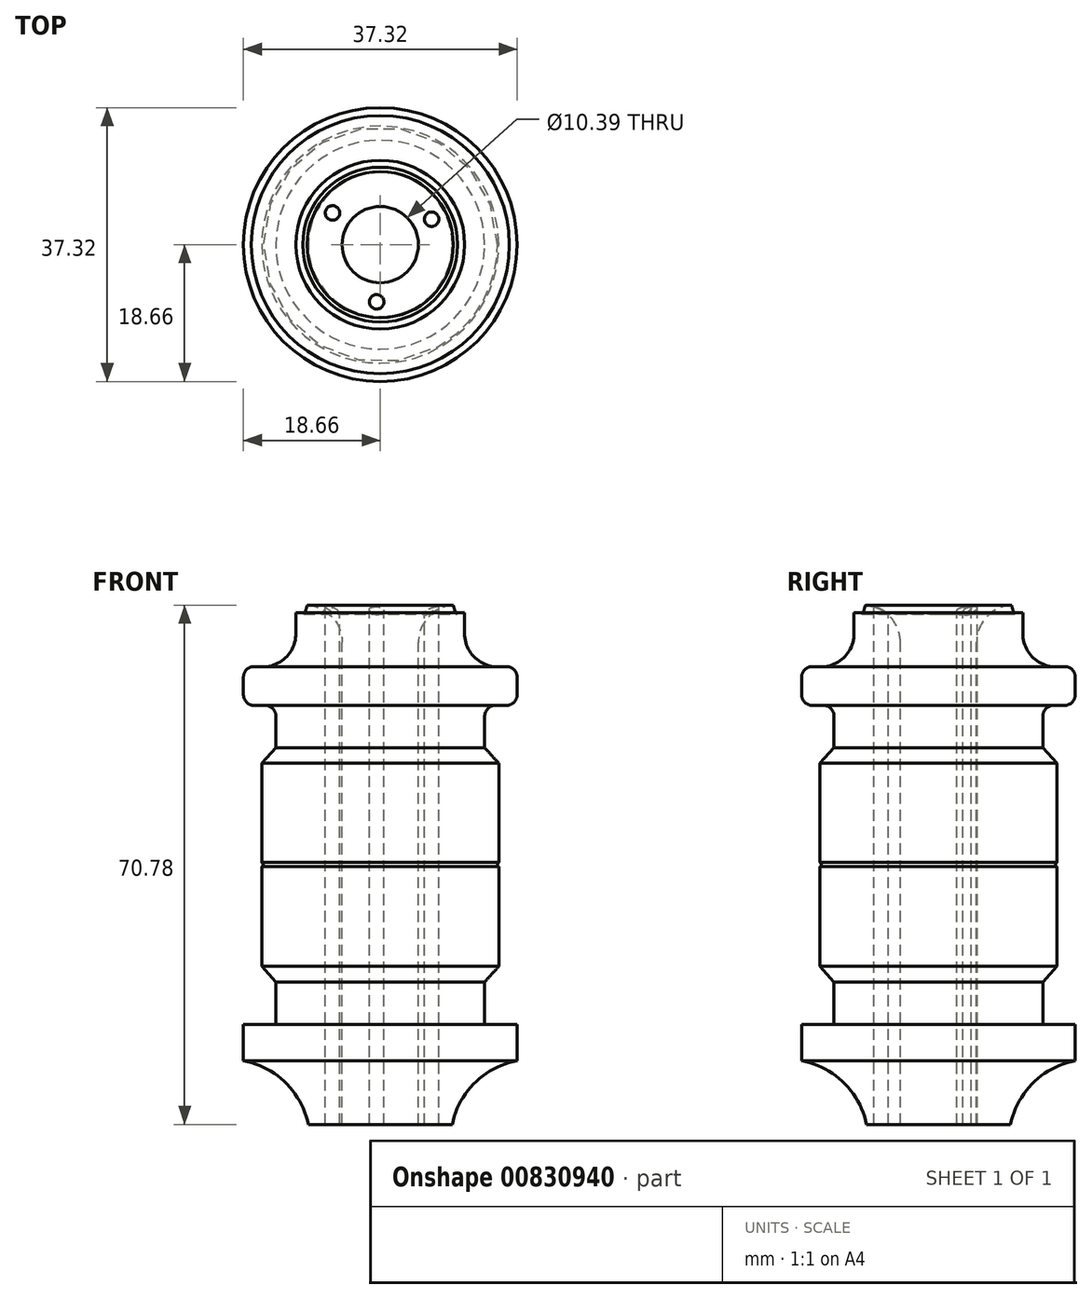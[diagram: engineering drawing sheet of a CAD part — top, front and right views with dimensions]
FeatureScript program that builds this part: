
annotation { "Feature Type Name" : "Feature", "Feature Type Description" : "" }
export const myFeature = defineFeature(function(context is Context, id is Id, definition is map)
    precondition{}
    {
        {
            var Q0;
            Q0=qCreatedBy(makeId("Front.planeOp"),FACE);
            var sketch = newSketch(context, id + "F0", { "sketchPlane" : qUnion([Q0])});
            skLineSegment(sketch, "E0", {"start": v(0, 60.68) * mm, "end": v(0, -59.14) * mm, "construction": true});
            skLineSegment(sketch, "E1", {"start": v(5.2, -59.14) * mm, "end": v(5.2, 60.68) * mm});
            skLineSegment(sketch, "E2", {"start": v(5.2, 60.68) * mm, "end": v(9.8, 60.68) * mm});
            skLineSegment(sketch, "E3", {"start": v(18.66, 50.86) * mm, "end": v(18.66, 48.5) * mm});
            skLineSegment(sketch, "E4", {"start": v(17.18, 47.03) * mm, "end": v(15.7, 47.03) * mm});
            skLineSegment(sketch, "E5", {"start": v(14.23, 45.55) * mm, "end": v(14.23, 41.26) * mm});
            skLineSegment(sketch, "E6", {"start": v(14.23, 41.26) * mm, "end": v(16.16, 39.14) * mm});
            skLineSegment(sketch, "E7", {"start": v(16.16, 39.14) * mm, "end": v(16.16, 25.6) * mm});
            skLineSegment(sketch, "E8.MirrorCS", {"start": v(5.2, -10.1) * mm, "end": v(9.8, -10.1) * mm});
            skLineSegment(sketch, "E9.MirrorCS", {"start": v(18.66, -1.44) * mm, "end": v(18.66, 3.56) * mm});
            skLineSegment(sketch, "E10.MirrorCS", {"start": v(18.66, 3.56) * mm, "end": v(14.23, 3.56) * mm});
            skLineSegment(sketch, "E11.MirrorCS", {"start": v(14.23, 9.33) * mm, "end": v(16.16, 11.44) * mm});
            skLineSegment(sketch, "E12.MirrorCS", {"start": v(16.16, 11.44) * mm, "end": v(16.16, 25.03) * mm});
            skLineSegment(sketch, "E13.MirrorCS", {"start": v(14.23, 3.56) * mm, "end": v(14.23, 9.33) * mm});
            skLineSegment(sketch, "E14.MirrorCS", {"start": v(5.2, 109.73) * mm, "end": v(5.2, -10.1) * mm});
            skArc(sketch, "E15.MirrorCS", {"start": v(9.8, -10.1) * mm, "mid": v(12.9, -4.42) * mm, "end": v(18.66, -1.44) * mm});
            skArc(sketch, "E16", {"start": v(16.16, 25.6) * mm, "mid": v(15.97, 25.31) * mm, "end": v(16.16, 25.03) * mm});
            skPoint(sketch, "E17.visualSharp", {"position": v(18.66, 52.03) * mm});
            skArc(sketch, "E17.filletArc", {"start": v(18.66, 50.86) * mm, "mid": v(18.36, 51.75) * mm, "end": v(17.59, 52.28) * mm});
            skPoint(sketch, "E18.visualSharp", {"position": v(18.66, 47.03) * mm});
            skArc(sketch, "E18.filletArc", {"start": v(17.18, 47.03) * mm, "mid": v(18.22, 47.46) * mm, "end": v(18.66, 48.5) * mm});
            skPoint(sketch, "E19.visualSharp", {"position": v(14.23, 47.03) * mm});
            skArc(sketch, "E19.filletArc", {"start": v(15.7, 47.03) * mm, "mid": v(14.66, 46.6) * mm, "end": v(14.23, 45.55) * mm});
            skLineSegment(sketch, "E20", {"start": v(17.59, 52.28) * mm, "end": v(16.05, 52.28) * mm});
            skLineSegment(sketch, "E21", {"start": v(11.5, 56.83) * mm, "end": v(11.5, 59.66) * mm});
            skLineSegment(sketch, "E22", {"start": v(11.5, 59.66) * mm, "end": v(10.55, 59.66) * mm});
            skLineSegment(sketch, "E23", {"start": v(9.8, 60.68) * mm, "end": v(9.96, 60.68) * mm});
            skFitSpline(sketch, "E24", {"points": [v(9.96, 60.68) * mm, v(10.12, 60.14) * mm, v(10.24, 59.77) * mm, v(10.38, 59.49) * mm, v(10.48, 59.54) * mm, v(10.55, 59.66) * mm], "startDerivative": vector(0.57, -2.02) * mm, "endDerivative": vector(0.43, 0.87) * mm});
            skPoint(sketch, "E25.visualSharp", {"position": v(11.5, 52.28) * mm});
            skArc(sketch, "E25.filletArc", {"start": v(11.5, 56.83) * mm, "mid": v(12.83, 53.6) * mm, "end": v(16.05, 52.28) * mm});
            skSolve(sketch);
        }
        {
            var Q0;
            {var subQ2=sQuery(id+"F0.wireOp",EDGE,"E2");Q0=makeQuery(id+"F0.imprint","IMPRINT",FACE,{"disambiguationData":[TD([[makeQuery(id+"F0.imprint","IMPRINT",EDGE,{"derivedFrom":subQ2}),-1.0]])]});}
            var Q1;
            Q1=sQuery(id+"F0.wireOp",EDGE,"E0");
            revolve(context, id + "F1", {"surfaceOperationType" : NewSurfaceOperationType.NEW, "entities" : qUnion([Q0]), "axis" : qUnion([Q1]), "revolveType" : RevolveType.FULL});
        }
        {
            var Q0;
            Q0=makeQuery(id+"F1.opRevolve","SWEPT_FACE",FACE,{"disambiguationData":[OSD([sQuery(id+"F0.wireOp",EDGE,"E2"),sQuery(id+"F0.wireOp",EDGE,"E23")])]});
            var sketch = newSketch(context, id + "F2", { "sketchPlane" : qUnion([Q0])});
            skCircle(sketch, "E26", {"center": v(7, 3.47) * mm, "radius": 1 * mm});
            skCircle(sketch, "E27.1.0", {"center": v(-0.5, -7.8) * mm, "radius": 1 * mm});
            skCircle(sketch, "E27.2.0", {"center": v(-6.5, 4.33) * mm, "radius": 1 * mm});
            skPoint(sketch, "E27.center", {"position": v(0, 0) * mm});
            skLineSegment(sketch, "E27.anchor1", {"start": v(0, 0) * mm, "end": v(7, 3.47) * mm, "construction": true});
            skLineSegment(sketch, "E27.anchor2", {"start": v(0, 0) * mm, "end": v(-6.5, 4.33) * mm, "construction": true});
            skSolve(sketch);
        }
        {
            var Q0;
            Q0=makeQuery(id+"F2.imprint","IMPRINT",FACE,{"disambiguationData":[TD([[makeQuery(id+"F2.imprint","IMPRINT",EDGE,{"derivedFrom":sQuery(id+"F2.wireOp",EDGE,"E27.2.0")}),1.0]])]});
            var Q1;
            Q1=makeQuery(id+"F2.imprint","IMPRINT",FACE,{"disambiguationData":[TD([[makeQuery(id+"F2.imprint","IMPRINT",EDGE,{"derivedFrom":sQuery(id+"F2.wireOp",EDGE,"E26")}),1.0]])]});
            var Q2;
            Q2=makeQuery(id+"F2.imprint","IMPRINT",FACE,{"disambiguationData":[TD([[makeQuery(id+"F2.imprint","IMPRINT",EDGE,{"derivedFrom":sQuery(id+"F2.wireOp",EDGE,"E27.1.0")}),1.0]])]});
            extrude(context, id + "F3", {"entities" : qUnion([Q0, Q1, Q2]), "operationType" : NewBodyOperationType.REMOVE, "oppositeDirection" : true, "depth" : 76.96 * mm, "offsetDistance" : 25.4 * mm});
        }
        {
            var Q0;
            Q0=makeQuery(id+"F1.opRevolve","SWEPT_EDGE",EDGE,{"disambiguationData":[OSD([sQuery(id+"F0.wireOp",EDGE,"E2"),sQuery(id+"F0.wireOp",EDGE,"E14.MirrorCS")])]});
            fillet(context, id + "F4", {"entities" : qUnion([Q0]), "radius" : 5.08 * mm, "tangentPropagation" : true, "allowEdgeOverflow" : false});
        }
    });
